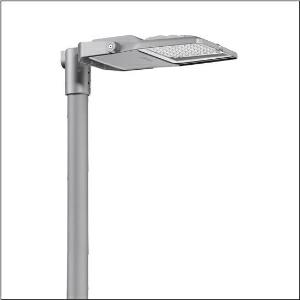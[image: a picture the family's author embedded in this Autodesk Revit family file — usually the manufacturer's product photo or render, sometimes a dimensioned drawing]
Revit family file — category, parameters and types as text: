
# Revit family: floodlight_fl_21_iq_mini___pl33t_5xa7771c2f3a_7d89
name_source: partatom
category: Lighting Fixtures
units: mm (PartAtom-declared; Revit-internal decimal feet)

## family parameters
Cut with Voids When Loaded = No
Host = Face
Light Source = No
Part Type = Normal
Room Calculation Point = No
Round Connector Dimension = Use Diameter
Shared = No

## types (1)
- --- (1 x LED, 12060 lm, 87.2 W, 3000K)
    Apparent Load = 87 VA
    CIE Flux Codes = 26 75 99 100 100
    Color Rendering = 70
    Color Temperature = 3000K
    Default Elevation = 1800 mm
    Description = Floodlight FL 21 iQ mini, floodlight, primary light control with lens, of PMMA, primary optical cover: protective disc, of toughened safety glass, transparent, light distribution: PL33T, light emission: direct distribution, installation type: surface-mounted, LED, High Power LED, rated luminous flux: 12.060lm, luminous efficacy: 138lm/W, light colour: 730, colour temperature: 3000K, control: Auto-Match, Temp-Guard, Lumen-Switch, Night-Set, Smart-Wire, Light-Fading, Desk-Remote (wireless, voltage-free reading and setting of iQ features in the workshop via application-optimized NFC function/RFID function), optimised constant luminous flux control (CLO 2.0), with terminal, 6-pole, mains connection: 220..240V, AC, 50/60Hz, start of lifetime: 87W, end of service life: 92W, reduction: 40W, luminaire housing, of diecast aluminium, powder-coated, Siteco® metallic grey (DB 702S), corrosivity category C5 mid according to DIN EN ISO 12944, sealing non-destructively replaceable, please order mast flange separately, mast bracket, of steel, galvanised, powder-coated, Siteco® metallic grey (DB 702S), protection rating (complete): IP66, insulation class (complete): insulation class II (safety insulation), certification: CE, ENEC, VDE, protection symbol: D, impact resistance: IK08, permissible operating ambient temperature: -40..+40°C, permissible operating ambient temperature for outdoor applications: -40..+50°C, standard: DIN EN 12944, LABS conformity tested according to VDMA 24364:2018-05, packaging unit: 1 piece

Light Distribution: PL33T
    Height = 70 mm
    Lamp = 1 x LED
    Lamp Light Flux = 12060 lm
    Lamp Power = 87.2 W
    Lamp count = 1
    Length = 485 mm
    Luminous efficacy = 138 lm/W
    Manufacturer = Siteco
    ModVariant = No
    Model = 5XA7771C2F3A
    Number of Poles = 1
    OnlyDefault = Yes
    Power Factor = 1
    Product Name = Floodlight FL 21 iQ mini | PL33T
    Product group = floodlight | pylon annexe
    ProductGroupID = 6200
    Protection Class = Protection class II
    Protection Degree = IP 66
    RLX_Detail_Level = 1
    RLX_Emergency_Light_Flux = 0 lm
    RLX_Emergency_Type = 0
    RLX_Emergency_Type_DB = No
    RlxData = <blob elided: 101137 chars, md5=fe8529cf>
    Socket = socket
    Standby Power = 0 W
    System Light Flux = 12060 lm
    System Power = 87 W
    Type Comments = factory setting: luminous flux: 100 % | dim-lin: 254 | 456 mA
    Type Image = l_1007125.jpg
    URL = http://relux.com
    VarID = @adj_099901
    Voltage = 0 V
    Weight = 0.00 kg
    Width = 337 mm

## geometry (parser evidence)
native form markers: Blend x4, Sweep x13
no freeform markers — native parametric forms only
